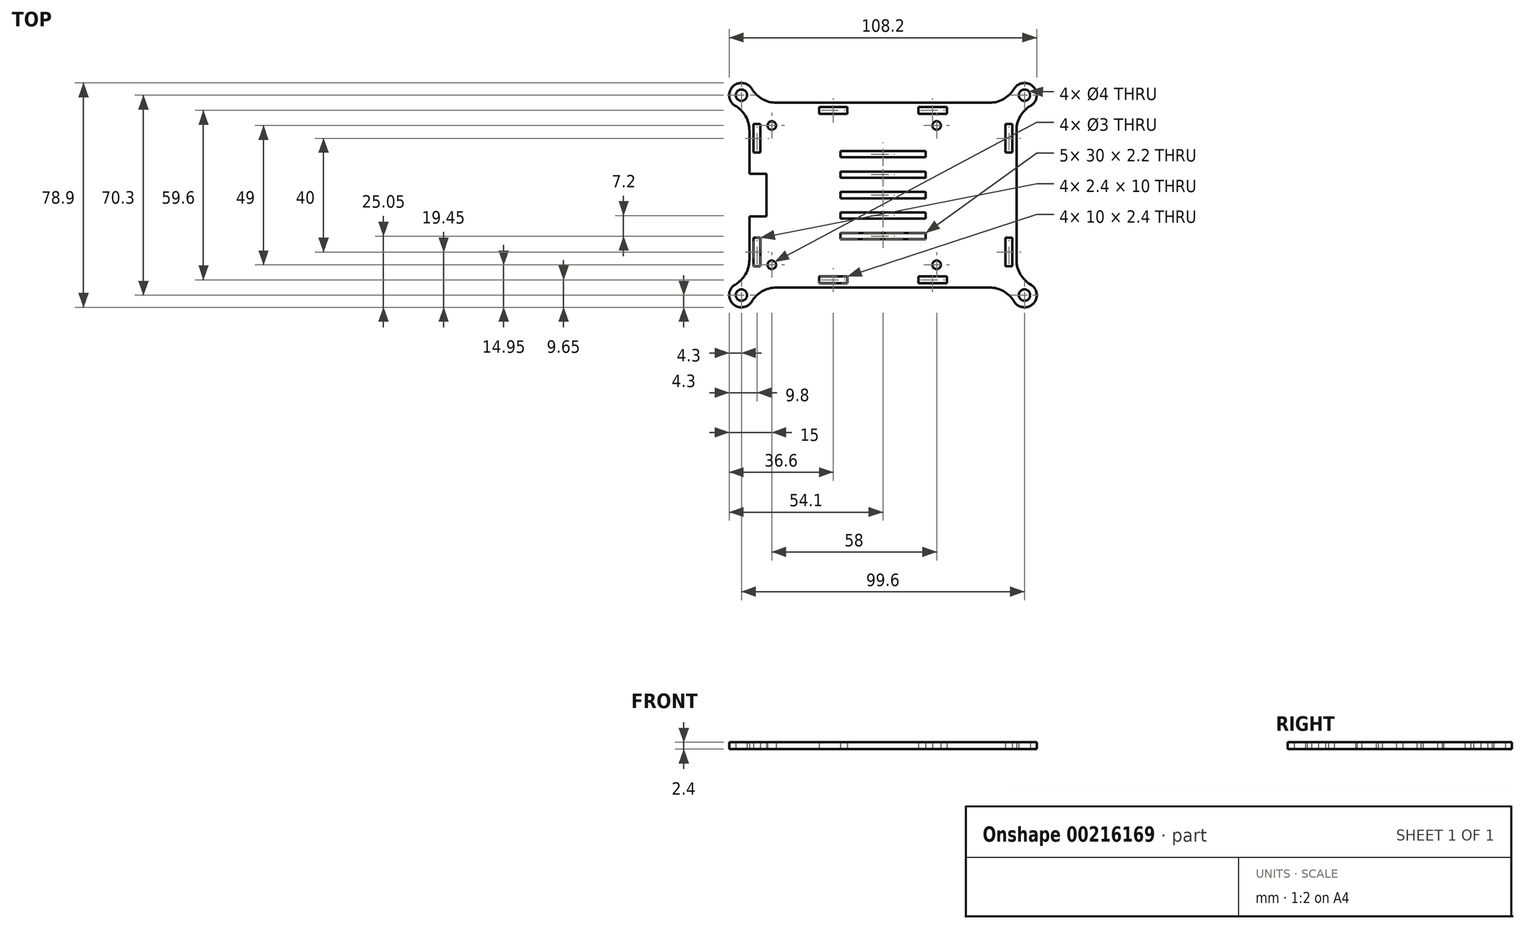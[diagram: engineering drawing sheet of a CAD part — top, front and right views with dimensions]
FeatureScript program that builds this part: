
annotation { "Feature Type Name" : "Feature", "Feature Type Description" : "" }
export const myFeature = defineFeature(function(context is Context, id is Id, definition is map)
    precondition{}
    {
        {
            var Q0;
            Q0=qCreatedBy(makeId("Top.planeOp"),FACE);
            var sketch = newSketch(context, id + "F0", { "sketchPlane" : qUnion([Q0])});
            skLineSegment(sketch, "E0.bottom", {"start": v(37.53, 32.5) * mm, "end": v(-37.53, 32.5) * mm});
            skLineSegment(sketch, "E0.top", {"start": v(37.53, -32.5) * mm, "end": v(-37.53, -32.5) * mm});
            skLineSegment(sketch, "E0.left", {"start": v(47, 22.8) * mm, "end": v(47, -22.8) * mm});
            skLineSegment(sketch, "E0.right", {"start": v(-47, 22.8) * mm, "end": v(-47, 7.5) * mm});
            skPoint(sketch, "E0.middle", {"position": v(0, 0) * mm});
            skCircle(sketch, "E1", {"center": v(-49.8, 35.15) * mm, "radius": 2 * mm});
            skArc(sketch, "E2", {"start": v(-46.11, 37.36) * mm, "mid": v(-52.86, 38.17) * mm, "end": v(-51.97, 31.43) * mm});
            skCircle(sketch, "E3", {"center": v(49.8, 35.15) * mm, "radius": 2 * mm});
            skArc(sketch, "E4", {"start": v(51.97, 31.43) * mm, "mid": v(52.86, 38.17) * mm, "end": v(46.11, 37.36) * mm});
            skCircle(sketch, "E5", {"center": v(49.8, -35.15) * mm, "radius": 2 * mm});
            skArc(sketch, "E6", {"start": v(46.11, -37.36) * mm, "mid": v(52.86, -38.17) * mm, "end": v(51.97, -31.43) * mm});
            skCircle(sketch, "E7", {"center": v(-49.8, -35.15) * mm, "radius": 2 * mm});
            skArc(sketch, "E8", {"start": v(-51.97, -31.43) * mm, "mid": v(-52.86, -38.17) * mm, "end": v(-46.11, -37.36) * mm});
            skPoint(sketch, "E9.orphan", {"position": v(-47, 32.5) * mm});
            skPoint(sketch, "E10.visualSharp", {"position": v(-46.41, 32.5) * mm});
            skArc(sketch, "E10.filletArc", {"start": v(-46.11, 37.36) * mm, "mid": v(-42.46, 33.8) * mm, "end": v(-37.53, 32.5) * mm});
            skPoint(sketch, "E11.visualSharp", {"position": v(-47, 31.89) * mm});
            skArc(sketch, "E11.filletArc", {"start": v(-47, 22.8) * mm, "mid": v(-48.33, 27.78) * mm, "end": v(-51.97, 31.43) * mm});
            skPoint(sketch, "E12.orphan", {"position": v(47, 32.5) * mm});
            skPoint(sketch, "E13.orphan", {"position": v(47, -32.5) * mm});
            skPoint(sketch, "E14.orphan", {"position": v(-47, -32.5) * mm});
            skPoint(sketch, "E15.visualSharp", {"position": v(-46.41, -32.5) * mm});
            skArc(sketch, "E15.filletArc", {"start": v(-37.53, -32.5) * mm, "mid": v(-42.46, -33.8) * mm, "end": v(-46.11, -37.36) * mm});
            skPoint(sketch, "E16.visualSharp", {"position": v(-47, -31.89) * mm});
            skArc(sketch, "E16.filletArc", {"start": v(-51.97, -31.43) * mm, "mid": v(-48.33, -27.78) * mm, "end": v(-47, -22.8) * mm});
            skPoint(sketch, "E17.visualSharp", {"position": v(46.41, -32.5) * mm});
            skArc(sketch, "E17.filletArc", {"start": v(46.11, -37.36) * mm, "mid": v(42.46, -33.8) * mm, "end": v(37.53, -32.5) * mm});
            skPoint(sketch, "E18.visualSharp", {"position": v(47, -31.89) * mm});
            skArc(sketch, "E18.filletArc", {"start": v(47, -22.8) * mm, "mid": v(48.33, -27.78) * mm, "end": v(51.97, -31.43) * mm});
            skPoint(sketch, "E19.visualSharp", {"position": v(47, 31.89) * mm});
            skArc(sketch, "E19.filletArc", {"start": v(51.97, 31.43) * mm, "mid": v(48.33, 27.78) * mm, "end": v(47, 22.8) * mm});
            skPoint(sketch, "E20.visualSharp", {"position": v(46.41, 32.5) * mm});
            skArc(sketch, "E20.filletArc", {"start": v(37.53, 32.5) * mm, "mid": v(42.46, 33.8) * mm, "end": v(46.11, 37.36) * mm});
            skCircle(sketch, "E21", {"center": v(-39.1, 24.5) * mm, "radius": 1.5 * mm});
            skCircle(sketch, "E22", {"center": v(18.9, 24.5) * mm, "radius": 1.5 * mm});
            skCircle(sketch, "E23", {"center": v(-39.1, -24.5) * mm, "radius": 1.5 * mm});
            skCircle(sketch, "E24", {"center": v(18.9, -24.5) * mm, "radius": 1.5 * mm});
            skLineSegment(sketch, "E25.bottom", {"start": v(-41, 7.5) * mm, "end": v(-47, 7.5) * mm});
            skLineSegment(sketch, "E25.top", {"start": v(-41, -7.5) * mm, "end": v(-47, -7.5) * mm});
            skLineSegment(sketch, "E25.left", {"start": v(-41, 7.5) * mm, "end": v(-41, -7.5) * mm});
            skPoint(sketch, "E25.middle", {"position": v(-47, 0) * mm});
            skPoint(sketch, "E25.right.start.orphan", {"position": v(-53, 7.5) * mm});
            skPoint(sketch, "E26.orphan", {"position": v(-53, -7.5) * mm});
            skLineSegment(sketch, "E27.trimOffspring", {"start": v(-47, -7.5) * mm, "end": v(-47, -22.8) * mm});
            skLineSegment(sketch, "E28.bottom", {"start": v(15, 1.1) * mm, "end": v(-15, 1.1) * mm});
            skLineSegment(sketch, "E28.top", {"start": v(15, -1.1) * mm, "end": v(-15, -1.1) * mm});
            skLineSegment(sketch, "E28.left", {"start": v(15, 1.1) * mm, "end": v(15, -1.1) * mm});
            skLineSegment(sketch, "E28.right", {"start": v(-15, 1.1) * mm, "end": v(-15, -1.1) * mm});
            skPoint(sketch, "E29.middle", {"position": v(0, 7.2) * mm});
            skLineSegment(sketch, "E30.bottom", {"start": v(15, 8.3) * mm, "end": v(-15, 8.3) * mm});
            skLineSegment(sketch, "E30.top", {"start": v(15, 6.1) * mm, "end": v(-15, 6.1) * mm});
            skLineSegment(sketch, "E30.left", {"start": v(15, 8.3) * mm, "end": v(15, 6.1) * mm});
            skLineSegment(sketch, "E30.right", {"start": v(-15, 8.3) * mm, "end": v(-15, 6.1) * mm});
            skPoint(sketch, "E31.middle", {"position": v(0, 14.4) * mm});
            skLineSegment(sketch, "E32.bottom", {"start": v(15, 15.5) * mm, "end": v(-15, 15.5) * mm});
            skLineSegment(sketch, "E32.top", {"start": v(15, 13.3) * mm, "end": v(-15, 13.3) * mm});
            skLineSegment(sketch, "E32.left", {"start": v(15, 15.5) * mm, "end": v(15, 13.3) * mm});
            skLineSegment(sketch, "E32.right", {"start": v(-15, 15.5) * mm, "end": v(-15, 13.3) * mm});
            skPoint(sketch, "E33.middle", {"position": v(0, -7.2) * mm});
            skLineSegment(sketch, "E34.bottom", {"start": v(15, -6.1) * mm, "end": v(-15, -6.1) * mm});
            skLineSegment(sketch, "E34.top", {"start": v(15, -8.3) * mm, "end": v(-15, -8.3) * mm});
            skLineSegment(sketch, "E34.left", {"start": v(15, -6.1) * mm, "end": v(15, -8.3) * mm});
            skLineSegment(sketch, "E34.right", {"start": v(-15, -6.1) * mm, "end": v(-15, -8.3) * mm});
            skPoint(sketch, "E35.middle", {"position": v(0, -14.4) * mm});
            skLineSegment(sketch, "E36.bottom", {"start": v(15, -13.3) * mm, "end": v(-15, -13.3) * mm});
            skLineSegment(sketch, "E36.top", {"start": v(15, -15.5) * mm, "end": v(-15, -15.5) * mm});
            skLineSegment(sketch, "E36.left", {"start": v(15, -13.3) * mm, "end": v(15, -15.5) * mm});
            skLineSegment(sketch, "E36.right", {"start": v(-15, -13.3) * mm, "end": v(-15, -15.5) * mm});
            skLineSegment(sketch, "E37.bottom", {"start": v(-22.5, 31) * mm, "end": v(-12.5, 31) * mm});
            skLineSegment(sketch, "E37.top", {"start": v(-22.5, 28.6) * mm, "end": v(-12.5, 28.6) * mm});
            skLineSegment(sketch, "E37.left", {"start": v(-22.5, 31) * mm, "end": v(-22.5, 28.6) * mm});
            skLineSegment(sketch, "E37.right", {"start": v(-12.5, 31) * mm, "end": v(-12.5, 28.6) * mm});
            skLineSegment(sketch, "E38.bottom", {"start": v(12.5, 31) * mm, "end": v(22.5, 31) * mm});
            skLineSegment(sketch, "E38.top", {"start": v(12.5, 28.6) * mm, "end": v(22.5, 28.6) * mm});
            skLineSegment(sketch, "E38.left", {"start": v(12.5, 31) * mm, "end": v(12.5, 28.6) * mm});
            skLineSegment(sketch, "E38.right", {"start": v(22.5, 31) * mm, "end": v(22.5, 28.6) * mm});
            skLineSegment(sketch, "E39.bottom", {"start": v(43.1, 25) * mm, "end": v(45.5, 25) * mm});
            skLineSegment(sketch, "E39.top", {"start": v(43.1, 15) * mm, "end": v(45.5, 15) * mm});
            skLineSegment(sketch, "E39.left", {"start": v(43.1, 25) * mm, "end": v(43.1, 15) * mm});
            skLineSegment(sketch, "E39.right", {"start": v(45.5, 25) * mm, "end": v(45.5, 15) * mm});
            skLineSegment(sketch, "E40.bottom", {"start": v(43.1, -15) * mm, "end": v(45.5, -15) * mm});
            skLineSegment(sketch, "E40.top", {"start": v(43.1, -25) * mm, "end": v(45.5, -25) * mm});
            skLineSegment(sketch, "E40.left", {"start": v(43.1, -15) * mm, "end": v(43.1, -25) * mm});
            skLineSegment(sketch, "E40.right", {"start": v(45.5, -15) * mm, "end": v(45.5, -25) * mm});
            skLineSegment(sketch, "E41.bottom", {"start": v(12.5, -28.6) * mm, "end": v(22.5, -28.6) * mm});
            skLineSegment(sketch, "E41.top", {"start": v(12.5, -31) * mm, "end": v(22.5, -31) * mm});
            skLineSegment(sketch, "E41.left", {"start": v(12.5, -28.6) * mm, "end": v(12.5, -31) * mm});
            skLineSegment(sketch, "E41.right", {"start": v(22.5, -28.6) * mm, "end": v(22.5, -31) * mm});
            skLineSegment(sketch, "E42.bottom", {"start": v(-22.5, -28.6) * mm, "end": v(-12.5, -28.6) * mm});
            skLineSegment(sketch, "E42.top", {"start": v(-22.5, -31) * mm, "end": v(-12.5, -31) * mm});
            skLineSegment(sketch, "E42.left", {"start": v(-22.5, -28.6) * mm, "end": v(-22.5, -31) * mm});
            skLineSegment(sketch, "E42.right", {"start": v(-12.5, -28.6) * mm, "end": v(-12.5, -31) * mm});
            skLineSegment(sketch, "E43.bottom", {"start": v(-45.5, 25) * mm, "end": v(-43.1, 25) * mm});
            skLineSegment(sketch, "E43.top", {"start": v(-45.5, 15) * mm, "end": v(-43.1, 15) * mm});
            skLineSegment(sketch, "E43.left", {"start": v(-45.5, 25) * mm, "end": v(-45.5, 15) * mm});
            skLineSegment(sketch, "E43.right", {"start": v(-43.1, 25) * mm, "end": v(-43.1, 15) * mm});
            skPoint(sketch, "E44.oppositeSnap0", {"position": v(-43.1, 20) * mm});
            skLineSegment(sketch, "E44.bottom", {"start": v(-45.5, -15) * mm, "end": v(-43.1, -15) * mm});
            skLineSegment(sketch, "E44.top", {"start": v(-45.5, -25) * mm, "end": v(-43.1, -25) * mm});
            skLineSegment(sketch, "E44.left", {"start": v(-45.5, -15) * mm, "end": v(-45.5, -25) * mm});
            skLineSegment(sketch, "E44.right", {"start": v(-43.1, -15) * mm, "end": v(-43.1, -25) * mm});
            skSolve(sketch);
        }
        {
            var Q0;
            Q0 = qSketchRegion(id + "F0", true);
            extrude(context, id + "F1", {"entities" : qUnion([Q0]), "depth" : 2.4 * mm});
        }
    });
